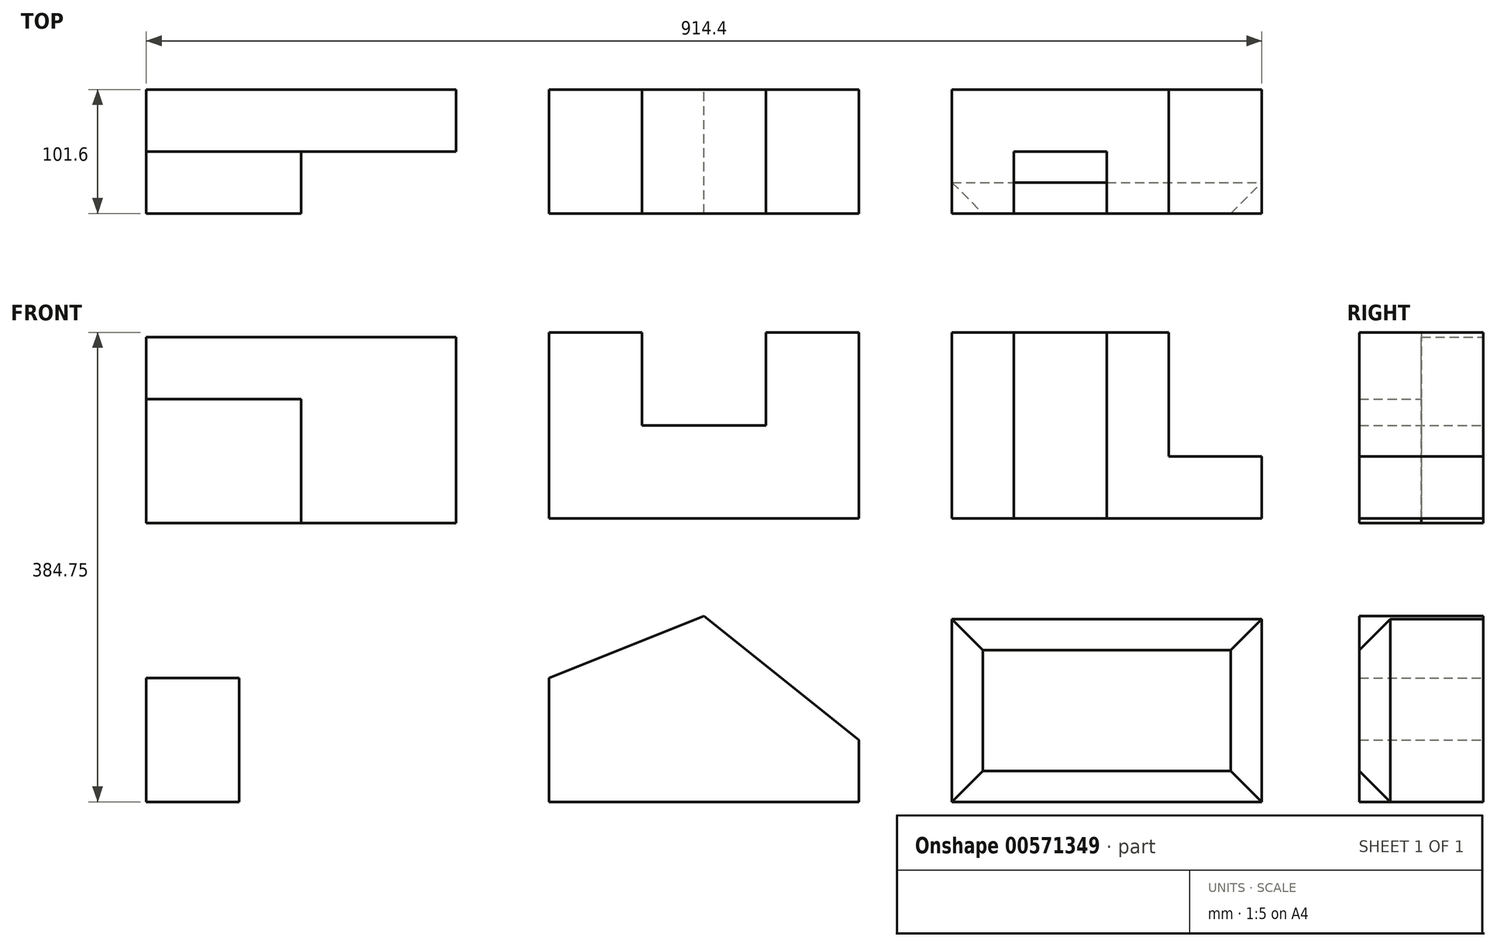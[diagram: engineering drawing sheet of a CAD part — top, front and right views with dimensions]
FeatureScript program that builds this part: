
annotation { "Feature Type Name" : "Feature", "Feature Type Description" : "" }
export const myFeature = defineFeature(function(context is Context, id is Id, definition is map)
    precondition{}
    {
        {
            var Q0;
            Q0=qCreatedBy(makeId("Front.planeOp"),FACE);
            var sketch = newSketch(context, id + "F0", { "sketchPlane" : qUnion([Q0])});
            skLineSegment(sketch, "E0", {"start": v(0, 0) * mm, "end": v(254, 0) * mm});
            skLineSegment(sketch, "E1", {"start": v(0, 0) * mm, "end": v(0, 152.4) * mm});
            skPoint(sketch, "E2.endSnap0", {"position": v(0, 76.2) * mm});
            skLineSegment(sketch, "E3", {"start": v(0, 152.4) * mm, "end": v(76.2, 152.4) * mm});
            skLineSegment(sketch, "E4", {"start": v(177.8, 76.2) * mm, "end": v(76.2, 76.2) * mm});
            skLineSegment(sketch, "E5", {"start": v(76.2, 152.4) * mm, "end": v(76.2, 76.2) * mm});
            skLineSegment(sketch, "E6", {"start": v(254, 0) * mm, "end": v(254, 152.4) * mm});
            skLineSegment(sketch, "E7", {"start": v(254, 152.4) * mm, "end": v(177.8, 152.4) * mm});
            skLineSegment(sketch, "E8", {"start": v(177.8, 152.4) * mm, "end": v(177.8, 76.2) * mm});
            skLineSegment(sketch, "E9.bottom", {"start": v(-76.2, -3.75) * mm, "end": v(-330.2, -3.75) * mm});
            skLineSegment(sketch, "E9.top", {"start": v(-76.2, 148.65) * mm, "end": v(-330.2, 148.65) * mm});
            skLineSegment(sketch, "E9.left", {"start": v(-76.2, -3.75) * mm, "end": v(-76.2, 148.65) * mm});
            skLineSegment(sketch, "E9.right", {"start": v(-330.2, -3.75) * mm, "end": v(-330.2, 148.65) * mm});
            skLineSegment(sketch, "E10", {"start": v(-330.2, 97.85) * mm, "end": v(-203.2, 97.85) * mm});
            skLineSegment(sketch, "E11", {"start": v(-203.2, 97.85) * mm, "end": v(-203.2, -3.75) * mm});
            skLineSegment(sketch, "E12", {"start": v(330.2, 152.4) * mm, "end": v(508, 152.4) * mm});
            skLineSegment(sketch, "E13", {"start": v(508, 152.4) * mm, "end": v(508, 50.8) * mm});
            skLineSegment(sketch, "E14", {"start": v(508, 50.8) * mm, "end": v(584.2, 50.8) * mm});
            skLineSegment(sketch, "E15", {"start": v(584.2, 50.8) * mm, "end": v(584.2, 0) * mm});
            skLineSegment(sketch, "E16", {"start": v(330.2, 152.4) * mm, "end": v(330.2, 0) * mm});
            skLineSegment(sketch, "E17", {"start": v(330.2, 0) * mm, "end": v(584.2, 0) * mm});
            skLineSegment(sketch, "E18.bottom", {"start": v(-330.2, -79.95) * mm, "end": v(-76.2, -79.95) * mm});
            skLineSegment(sketch, "E18.top", {"start": v(-330.2, -232.35) * mm, "end": v(-76.2, -232.35) * mm});
            skLineSegment(sketch, "E18.left", {"start": v(-330.2, -79.95) * mm, "end": v(-330.2, -232.35) * mm});
            skLineSegment(sketch, "E18.right", {"start": v(-76.2, -79.95) * mm, "end": v(-76.2, -232.35) * mm});
            skLineSegment(sketch, "E19", {"start": v(-330.2, -232.35) * mm, "end": v(-330.2, -130.75) * mm});
            skLineSegment(sketch, "E20", {"start": v(-330.2, -130.75) * mm, "end": v(-254, -130.75) * mm});
            skLineSegment(sketch, "E21", {"start": v(-254, -130.75) * mm, "end": v(-254, -232.35) * mm});
            skLineSegment(sketch, "E22", {"start": v(-76.2, -79.95) * mm, "end": v(-76.2, -181.55) * mm});
            skLineSegment(sketch, "E23", {"start": v(-76.2, -181.55) * mm, "end": v(-152.4, -181.55) * mm});
            skLineSegment(sketch, "E24", {"start": v(-152.4, -181.55) * mm, "end": v(-152.4, -79.95) * mm});
            skLineSegment(sketch, "E25", {"start": v(-76.2, -79.95) * mm, "end": v(0, -79.95) * mm});
            skLineSegment(sketch, "E26.bottom", {"start": v(0, -79.95) * mm, "end": v(254, -79.95) * mm});
            skLineSegment(sketch, "E26.top", {"start": v(0, -232.35) * mm, "end": v(254, -232.35) * mm});
            skLineSegment(sketch, "E26.left", {"start": v(0, -79.95) * mm, "end": v(0, -232.35) * mm});
            skLineSegment(sketch, "E26.right", {"start": v(254, -79.95) * mm, "end": v(254, -232.35) * mm});
            skLineSegment(sketch, "E27", {"start": v(0, -79.95) * mm, "end": v(0, -130.75) * mm});
            skLineSegment(sketch, "E28", {"start": v(254, -79.95) * mm, "end": v(254, -181.55) * mm});
            skLineSegment(sketch, "E29", {"start": v(0, -79.95) * mm, "end": v(127, -79.95) * mm});
            skLineSegment(sketch, "E30", {"start": v(127, -79.95) * mm, "end": v(0, -130.75) * mm});
            skLineSegment(sketch, "E31", {"start": v(127, -79.95) * mm, "end": v(254, -181.55) * mm});
            skLineSegment(sketch, "E32.top", {"start": v(330.2, -232.35) * mm, "end": v(584.2, -232.35) * mm});
            skLineSegment(sketch, "E32.left", {"start": v(330.2, -82.7) * mm, "end": v(330.2, -232.35) * mm});
            skLineSegment(sketch, "E32.right", {"start": v(584.2, -82.7) * mm, "end": v(584.2, -232.35) * mm});
            skLineSegment(sketch, "E33", {"start": v(330.2, -82.7) * mm, "end": v(584.2, -82.7) * mm});
            skSolve(sketch);
        }
        {
            var Q0;
            Q0=makeQuery(id+"F0.imprint","IMPRINT",FACE,{"disambiguationData":[TD([[makeQuery(id+"F0.imprint","IMPRINT",EDGE,{"derivedFrom":sQuery(id+"F0.wireOp",EDGE,"E0")}),1.0]])]});
            extrude(context, id + "F1", {"entities" : qUnion([Q0]), "depth" : 101.6 * mm, "offsetDistance" : 25.4 * mm});
        }
        {
            var Q0;
            {var subQ1=sQuery(id+"F0.wireOp",EDGE,"E9.top");Q0=makeQuery(id+"F0.imprint","IMPRINT",FACE,{"disambiguationData":[TD([[makeQuery(id+"F0.imprint","IMPRINT",EDGE,{"derivedFrom":subQ1}),1.0]])]});}
            extrude(context, id + "F2", {"entities" : qUnion([Q0]), "depth" : 50.8 * mm, "offsetDistance" : 25.4 * mm});
        }
        {
            var Q0;
            {var subQ4=sQuery(id+"F0.wireOp",EDGE,"E10");Q0=makeQuery(id+"F0.imprint","IMPRINT",FACE,{"disambiguationData":[TD([[makeQuery(id+"F0.imprint","IMPRINT",EDGE,{"derivedFrom":subQ4}),-1.0]])]});}
            extrude(context, id + "F3", {"entities" : qUnion([Q0]), "operationType" : NewBodyOperationType.ADD, "depth" : 101.6 * mm, "offsetDistance" : 25.4 * mm});
        }
        {
            var Q0;
            Q0=makeQuery(id+"F0.imprint","IMPRINT",FACE,{"disambiguationData":[TD([[makeQuery(id+"F0.imprint","IMPRINT",EDGE,{"derivedFrom":sQuery(id+"F0.wireOp",EDGE,"E12")}),-1.0]])]});
            extrude(context, id + "F4", {"entities" : qUnion([Q0]), "depth" : 101.6 * mm, "offsetDistance" : 25.4 * mm});
        }
        {
            var Q0;
            Q0=makeQuery(id+"F4.opExtrude","CAP_FACE",FACE,{"disambiguationData":[OSD([sQuery(id+"F0.wireOp",EDGE,"E12"),sQuery(id+"F0.wireOp",EDGE,"E13"),sQuery(id+"F0.wireOp",EDGE,"E14"),sQuery(id+"F0.wireOp",EDGE,"E15"),sQuery(id+"F0.wireOp",EDGE,"E16"),sQuery(id+"F0.wireOp",EDGE,"E17")])],"isStart":false});
            var sketch = newSketch(context, id + "F5", { "sketchPlane" : qUnion([Q0])});
            skLineSegment(sketch, "E34", {"start": v(381, 152.4) * mm, "end": v(381, 0) * mm});
            skLineSegment(sketch, "E35", {"start": v(457.2, 152.4) * mm, "end": v(457.2, 0) * mm});
            skSolve(sketch);
        }
        {
            var Q0;
            {var subQ0=sQuery(id+"F5.wireOp",EDGE,"E34");Q0=makeQuery(id+"F5.imprint","IMPRINT",FACE,{"disambiguationData":[TD([[makeQuery(id+"F5.imprint","IMPRINT",EDGE,{"derivedFrom":subQ0}),1.0]])]});}
            extrude(context, id + "F6", {"entities" : qUnion([Q0]), "operationType" : NewBodyOperationType.REMOVE, "oppositeDirection" : true, "depth" : 50.8 * mm, "offsetDistance" : 25.4 * mm});
        }
        {
            var Q0;
            {var subQ0=sQuery(id+"F0.wireOp",EDGE,"E18.left");Q0=makeQuery(id+"F0.imprint","IMPRINT",FACE,{"disambiguationData":[TD([[makeQuery(id+"F0.imprint","IMPRINT",EDGE,{"derivedFrom":subQ0}),1.0]])]});}
            extrude(context, id + "F7", {"entities" : qUnion([Q0]), "depth" : 101.6 * mm, "offsetDistance" : 25.4 * mm});
        }
        {
            var Q0;
            Q0=makeQuery(id+"F0.imprint","IMPRINT",FACE,{"disambiguationData":[TD([[makeQuery(id+"F0.imprint","IMPRINT",EDGE,{"derivedFrom":sQuery(id+"F0.wireOp",EDGE,"E26.top")}),1.0]])]});
            extrude(context, id + "F8", {"entities" : qUnion([Q0]), "depth" : 101.6 * mm, "offsetDistance" : 25.4 * mm});
        }
        {
            var Q0;
            Q0=makeQuery(id+"F0.imprint","IMPRINT",FACE,{"disambiguationData":[TD([[makeQuery(id+"F0.imprint","IMPRINT",EDGE,{"derivedFrom":sQuery(id+"F0.wireOp",EDGE,"E32.top")}),1.0]])]});
            extrude(context, id + "F9", {"entities" : qUnion([Q0]), "depth" : 101.6 * mm, "offsetDistance" : 25.4 * mm});
        }
        {
            var Q0;
            Q0=makeQuery(id+"F9.opExtrude","CAP_FACE",FACE,{"disambiguationData":[OSD([sQuery(id+"F0.wireOp",EDGE,"E32.top"),sQuery(id+"F0.wireOp",EDGE,"E32.left"),sQuery(id+"F0.wireOp",EDGE,"E32.right"),sQuery(id+"F0.wireOp",EDGE,"E33")])],"isStart":false});
            chamfer(context, id + "F10", {"entities" : qUnion([Q0]), "width" : 25.4 * mm, "tangentPropagation" : true});
        }
    });
